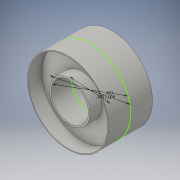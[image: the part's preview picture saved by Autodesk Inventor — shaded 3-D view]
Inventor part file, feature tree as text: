
AUTODESK INVENTOR PART (.ipt)
format: ipt  version: 2016 (Build 200138000, 138)  size: 129,536 bytes
history: native  units: in
note: dims shown in document units (in); Inventor stores cm internally (conversion verified against a paired STEP export)
features: extrude x4, fillet x2, sketch x1
ambient origin geometry x8: Origin, YZ Plane, XZ Plane, XY Plane, X Axis, Y Axis, Z Axis, Center Point
bodies: Solid1 (feature_tree)
feature tree (7):
  sketch  "Sketch1"  dims[d1=1.0in d2=0.98in d3=0.5in d4=0.24in d5=0.24in d6=0.0in d7=0.0in d8=0.27in d9=0.27in d10=0.0in d11=0.0in d12=0.1in d13=0.1in d14=0.0in d15=0.0in d16=0.25in d17=0.25in d18=0.0in d19=0.0in d20=0.001in d21=0.001in]
  extrude  "Extrusion1"  Depth=0.25in
  extrude  "Extrusion2"  Depth=0.5in
  extrude  "Extrusion3"  Depth=0.25in TaperAngle=0.0deg
  extrude  "Extrusion4"  Depth=0.27in TaperAngle=0.0deg
  fillet  "Fillet1"  Radius=0.1in
  fillet  "Fillet2"  Radius=0.25in
